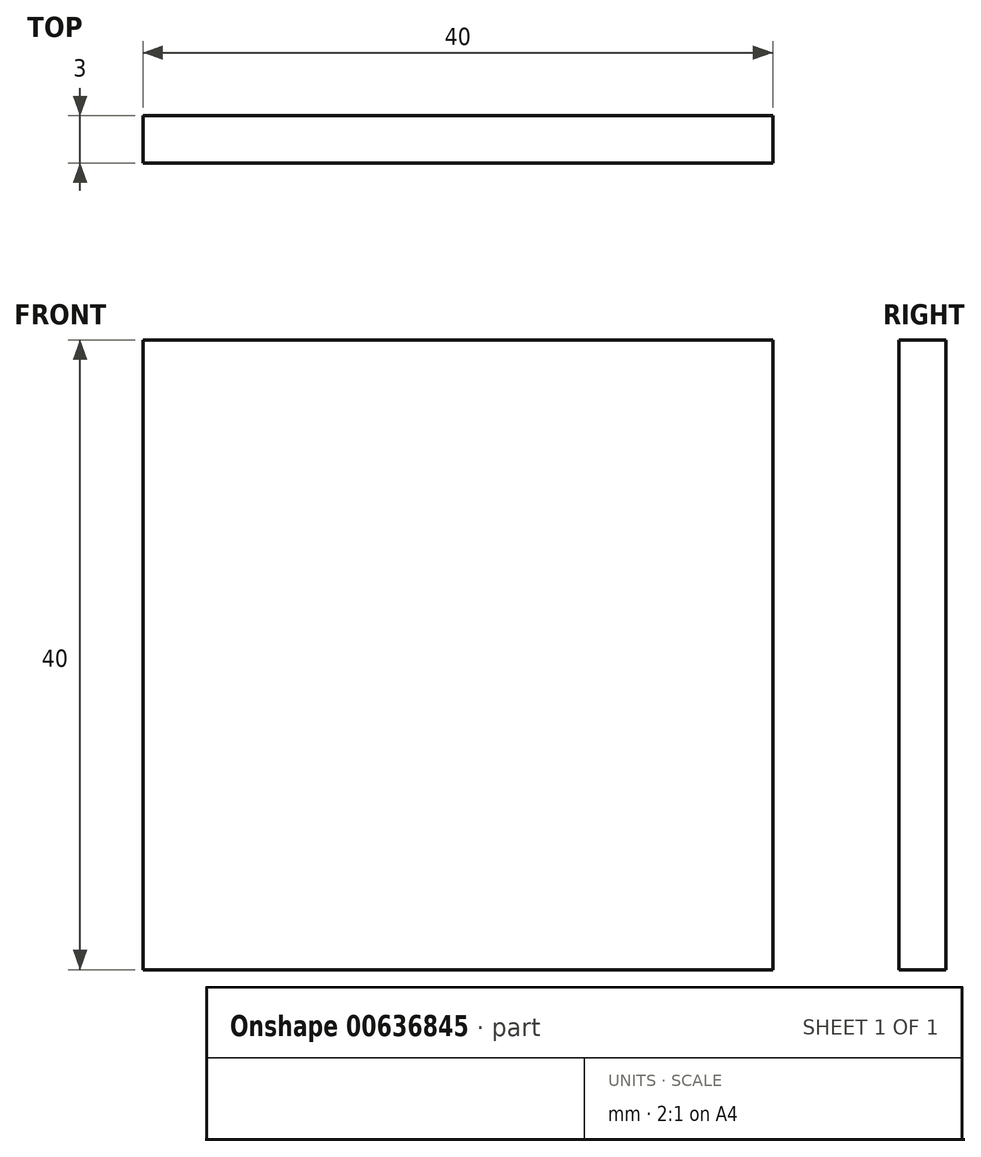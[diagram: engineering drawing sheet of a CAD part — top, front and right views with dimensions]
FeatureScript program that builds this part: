
annotation { "Feature Type Name" : "Feature", "Feature Type Description" : "" }
export const myFeature = defineFeature(function(context is Context, id is Id, definition is map)
    precondition{}
    {
        {
            var Q0;
            Q0=qCreatedBy(makeId("Front.planeOp"),FACE);
            var sketch = newSketch(context, id + "F0", { "sketchPlane" : qUnion([Q0])});
            skLineSegment(sketch, "E0.bottom", {"start": v(20, 20) * mm, "end": v(-20, 20) * mm});
            skLineSegment(sketch, "E0.top", {"start": v(20, -20) * mm, "end": v(-20, -20) * mm});
            skLineSegment(sketch, "E0.left", {"start": v(20, 20) * mm, "end": v(20, -20) * mm});
            skLineSegment(sketch, "E0.right", {"start": v(-20, 20) * mm, "end": v(-20, -20) * mm});
            skPoint(sketch, "E0.middle", {"position": v(0, 0) * mm});
            skSolve(sketch);
        }
        {
            var Q0;
            Q0=makeQuery(id+"F0.imprint","IMPRINT",FACE,{"disambiguationData":[TD([[makeQuery(id+"F0.imprint","IMPRINT",EDGE,{"derivedFrom":sQuery(id+"F0.wireOp",EDGE,"E0.bottom")}),1.0]])]});
            extrude(context, id + "F1", {"entities" : qUnion([Q0]), "depth" : 3 * mm, "offsetDistance" : 25 * mm});
        }
    });
